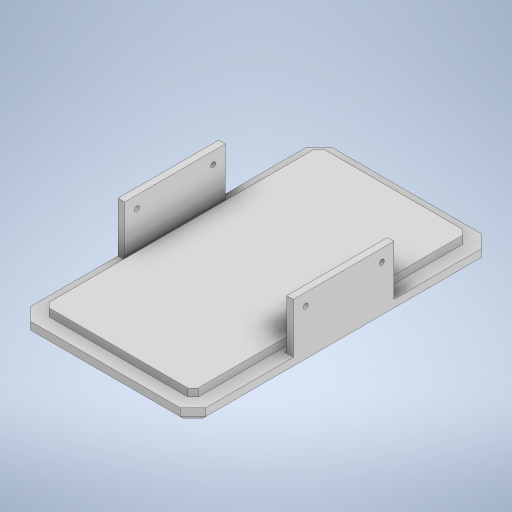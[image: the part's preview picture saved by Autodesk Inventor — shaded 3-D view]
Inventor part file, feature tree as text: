
AUTODESK INVENTOR PART (.ipt)
format: ipt  version: 2023 (Build 270158000, 158)  size: 291,328 bytes
history: native  units: mm
features: extrude x4, chamfer x3, sketch x2, other x1, fillet x1
ambient origin geometry x8: Origin, YZ Plane, XZ Plane, XY Plane, X Axis, Y Axis, Z Axis, Center Point
bodies: Body1 (feature_tree)
feature tree (11):
  other  "솔리드1"
  sketch  "스케치1"
  extrude  "돌출1"  Depth=58.6mm
  extrude  "돌출2"  Depth=108.2mm
  chamfer  "모따기1"  Distance=5.2mm
  extrude  "돌출3"  Depth=5.0mm TaperAngle=0.0deg
  extrude  "돌출4"  Depth=39.6mm
  chamfer  "모따기2"  Distance=19.7mm
  chamfer  "모따기3"  Distance=5.0mm Angle=45.0deg
  fillet  "모깎기2"  Radius=15.0mm
  sketch  "스케치2"
